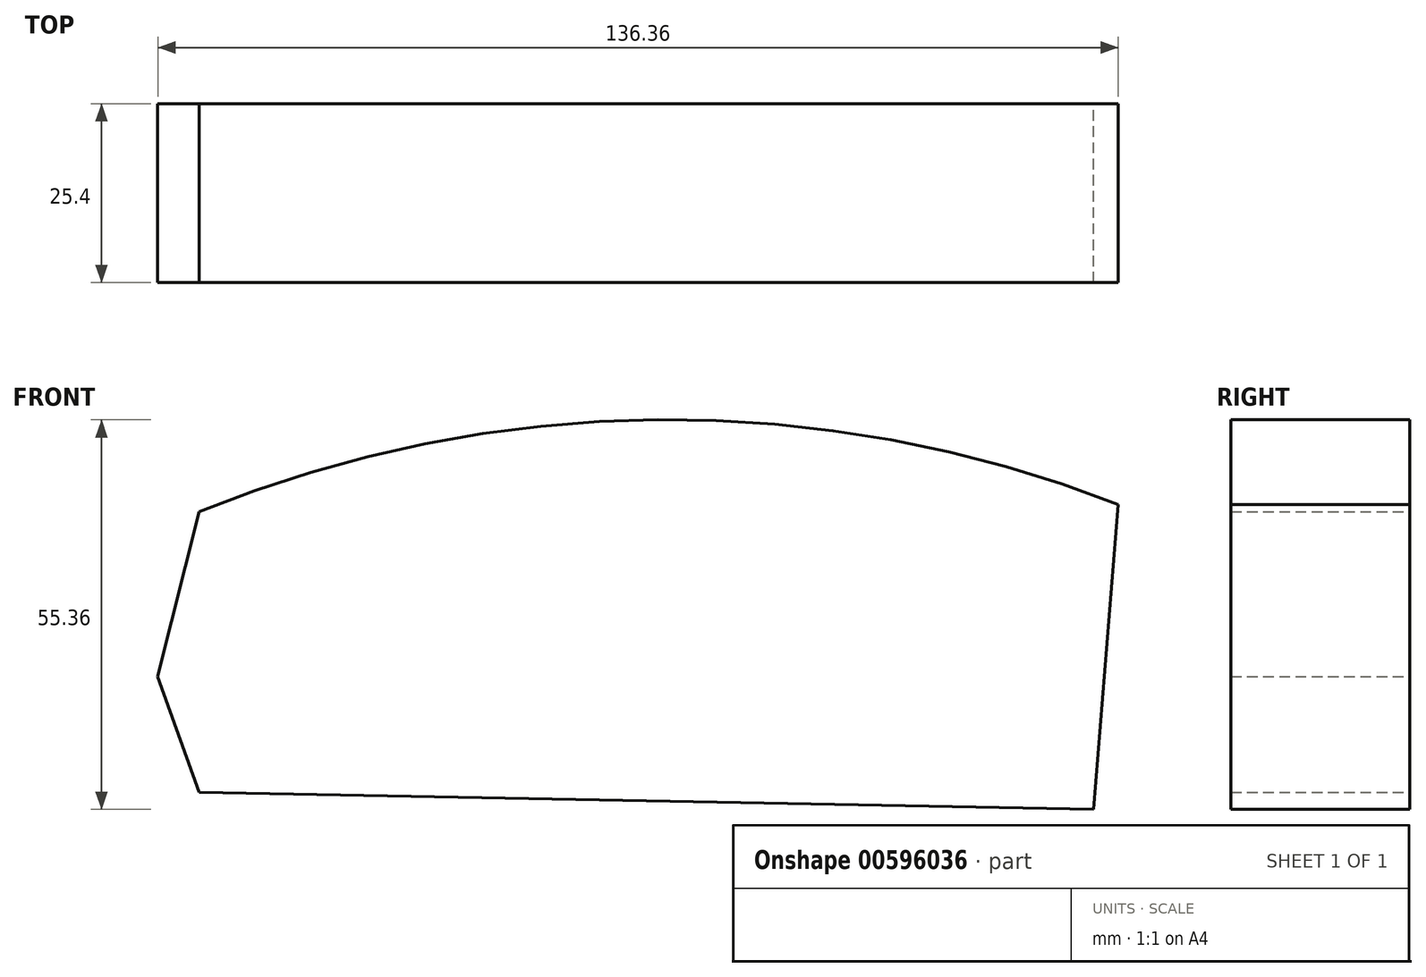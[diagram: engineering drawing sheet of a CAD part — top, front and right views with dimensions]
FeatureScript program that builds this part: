
annotation { "Feature Type Name" : "Feature", "Feature Type Description" : "" }
export const myFeature = defineFeature(function(context is Context, id is Id, definition is map)
    precondition{}
    {
        {
            var Q0;
            Q0=qCreatedBy(makeId("Front.planeOp"),FACE);
            var sketch = newSketch(context, id + "F0", { "sketchPlane" : qUnion([Q0])});
            skArc(sketch, "E0", {"start": v(65.99, 56.95) * mm, "mid": v(0.63, 68.97) * mm, "end": v(-64.53, 55.89) * mm});
            skLineSegment(sketch, "E1", {"start": v(-64.53, 55.89) * mm, "end": v(-70.37, 32.5) * mm});
            skLineSegment(sketch, "E2", {"start": v(-70.37, 32.5) * mm, "end": v(-64.53, 16.02) * mm});
            skLineSegment(sketch, "E3", {"start": v(-64.53, 16.02) * mm, "end": v(62.53, 13.62) * mm});
            skLineSegment(sketch, "E4", {"start": v(62.53, 13.62) * mm, "end": v(65.99, 56.95) * mm});
            skSolve(sketch);
        }
        {
            var Q0;
            Q0=makeQuery(id+"F0.imprint","IMPRINT",FACE,{"disambiguationData":[TD([[makeQuery(id+"F0.imprint","IMPRINT",EDGE,{"derivedFrom":sQuery(id+"F0.wireOp",EDGE,"E0")}),1.0]])]});
            extrude(context, id + "F1", {"entities" : qUnion([Q0]), "endBound" : BoundingType.SYMMETRIC, "depth" : 25.4 * mm, "offsetDistance" : 25.4 * mm});
        }
    });
